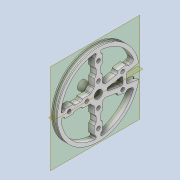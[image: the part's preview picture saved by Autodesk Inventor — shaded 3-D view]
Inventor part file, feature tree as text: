
AUTODESK INVENTOR PART (.ipt)
format: ipt  version: 2020 (Build 240168000, 168)  size: 719,872 bytes
history: native  units: mm
features: sketch x12, extrude x11, projected_geometry x8, fillet x7, plane x2, mirror x2, chamfer x2, thicken_offset x1, revolve x1
ambient origin geometry x8: Origin, YZ Plane, XZ Plane, XY Plane, X Axis, Y Axis, Z Axis, Center Point
bodies: Solid1 (feature_tree)
feature tree (46):
  extrude  "Extrusion1"  Depth=3.0mm
  extrude  "Extrusion2"  Depth=7.0mm
  extrude  "Extrusion3"  Depth=7.0mm
  extrude  "Extrusion4"  Depth=7.0mm
  extrude  "Extrusion5"  Depth=7.0mm
  plane  "Work Plane1"
  mirror  "Mirror1"
  extrude  "Extrusion6"  Depth=7.0mm
  extrude  "Extrusion7"  Depth=7.0mm
  extrude  "Extrusion8"  Depth=4.0mm
  thicken_offset  "Thicken1"
  plane  "Work Plane2"
  revolve  "Revolution1"  [1 undecoded]
  extrude  "Extrusion9"  Depth=7.0mm
  mirror  "Mirror2"
  fillet  "Fillet1"  Radius=7.0mm
  extrude  "Extrusion10"  Depth=4.0mm TaperAngle=0.0deg
  fillet  "Fillet2"  Radius=15.0mm
  fillet  "Fillet3"  Radius=4.0mm
  fillet  "Fillet4"  Radius=1.745329mm
  fillet  "Fillet5"  Radius=1.745329mm
  fillet  "Fillet6"  Radius=4.0mm
  fillet  "Fillet7"  Radius=4.0mm
  extrude  "Extrusion11"  Depth=4.0mm TaperAngle=0.0deg
  chamfer  "Chamfer2"  Distance=10.0mm
  chamfer  "Chamfer3"  Distance=6.0mm
  sketch  "Sketch1"  dims[d0=70.0mm d1=3.0mm]
  sketch  "Sketch2"  dims[d2=25.0mm d3=7.0mm]
  sketch  "Sketch3"  dims[d4=25.0mm d5=7.0mm]
  projected_geometry  "Projected Loop1"
  sketch  "Sketch4"  dims[d6=25.0mm d7=7.0mm]
  projected_geometry  "Projected Loop2"
  sketch  "Sketch5"  dims[d8=10.0mm d9=7.0mm]
  projected_geometry  "Projected Loop3"
  sketch  "Sketch6"  dims[d10=10.0mm d11=7.0mm]
  projected_geometry  "Projected Loop4"
  sketch  "Sketch7"  dims[d12=10.0mm d13=7.0mm]
  sketch  "Sketch8"  dims[d14=4.0mm d15=4.0mm]
  projected_geometry  "Projected Loop5"
  sketch  "Sketch9"  dims[d16=4.0mm d17=7.0mm]
  projected_geometry  "Projected Loop6"
  sketch  "Sketch10"  dims[d18=7.0mm d19=7.0mm d20=7.0mm]
  projected_geometry  "Projected Loop7"
  sketch  "Sketch11"  dims[d21=30.0mm d23=180.0deg d25=4.0mm d26=0.0mm d27=15.0mm d28=4.0mm d29=0.0mm d30=1.745329mm d31=1.745329mm d32=4.0mm d33=4.0mm]
  projected_geometry  "Projected Loop8"
  sketch  "Sketch12"  dims[d34=4.0mm d35=0.0mm d36=4.0mm d37=0.0mm d38=10.0mm d39=6.0mm d40=7.0mm d41=4.0mm d42=0.0mm d43=3.5mm d44=3.5mm d45=3.5mm d46=3.2mm d47=3.2mm d48=3.2mm d49=3.2mm d50=3.2mm d51=3.2mm d52=3.2mm d53=3.2mm d54=4.0mm d55=0.0mm d56=3.0mm d57=4.0mm d58=0.0mm d59=2.5mm d60=10.0mm d61=0.0mm d62=1.0mm d63=1.0mm d64=3.0mm d65=2.0mm d66=10.0mm d67=90.0deg d68=1.5mm d69=1.0mm d70=1.0mm d71=10.0mm d72=0.0mm d73=0.5mm d74=3.0mm d75=10.0mm d76=0.0mm d77=2.0mm d78=2.0mm d79=1.0mm d80=1.5mm d81=1.0mm d82=3.0mm d86=6.15mm d87=3.0mm d88=0.0mm d89=0.5mm d90=2.0mm d91=45.0deg d92=1.575mm d93=2.0mm d94=45.0deg]
note: 1 required parameter value undecoded (feature->parameter linkage not recoverable at this tier; creation-order binding heuristic only, values carry confidence <= 0.55)
